# Revit family: HL_Трап для подвалов_HL72N
name_source: partatom
category: Instalační zařizovací předměty
revit_build: Autodesk Revit 2016 (Build: 20161004_0715(x64)
units: mm (PartAtom-declared; Revit-internal decimal feet)

## family parameters
Bod výpočtu místnosti = Ano
Kóta kulaté spojky = Použít průměr
Nadpis OmniClass = Deck Waste Water Drains
Ořezat dutým tvarem při načtení = Ne
Sdílené = Ano
Typ součásti = Normální
Vždy vertikální = Ano
Založené na pracovní rovině = Ne
Číslo OmniClass = 23.70.50.21.24.14

## types (1)
- HL_Трап для подвалов_HL72N
    EAN = 9003076999729
    Klíčová poznámka = HL72N
    Komentáře k typům = Трап для подвалов DN110 горизонтальный 148х148мм/138х138мм
    Model = HL72N
    Popis = Трап для подвалов
    Připojení CW = Ne
    Připojení HW = Ne
    Připojení odpadu = Ano
    Připojení ventilace = Ne
    URL = http://www.hutterer-lechner.com
    Výrobce = HL Hutterer & Lechner GmbH
    ВЕС = 0,873 kg
    ВЫСОТА МОНТАЖА = 160 mm
    МАКСИМАЛЬНАЯ НАГРУЗКА КЛАССА = K3 - 300 kg
    МАТЕРИАЛ = PP
    НАСАДКА = 48-95 mm/ 148x148 mm
    НОМИНАЛЬНЫЙ ДИАМЕТР = 110 mm
    ПРОИЗВОДИТЕЛЬНОСТЬ = 1,67 l/s
    РАЗМЕР = DN110
    РЕШЁТКА = 138x138 mm/ V2A

## geometry (parser evidence)
native form markers: Sweep x2
no freeform markers — native parametric forms only
